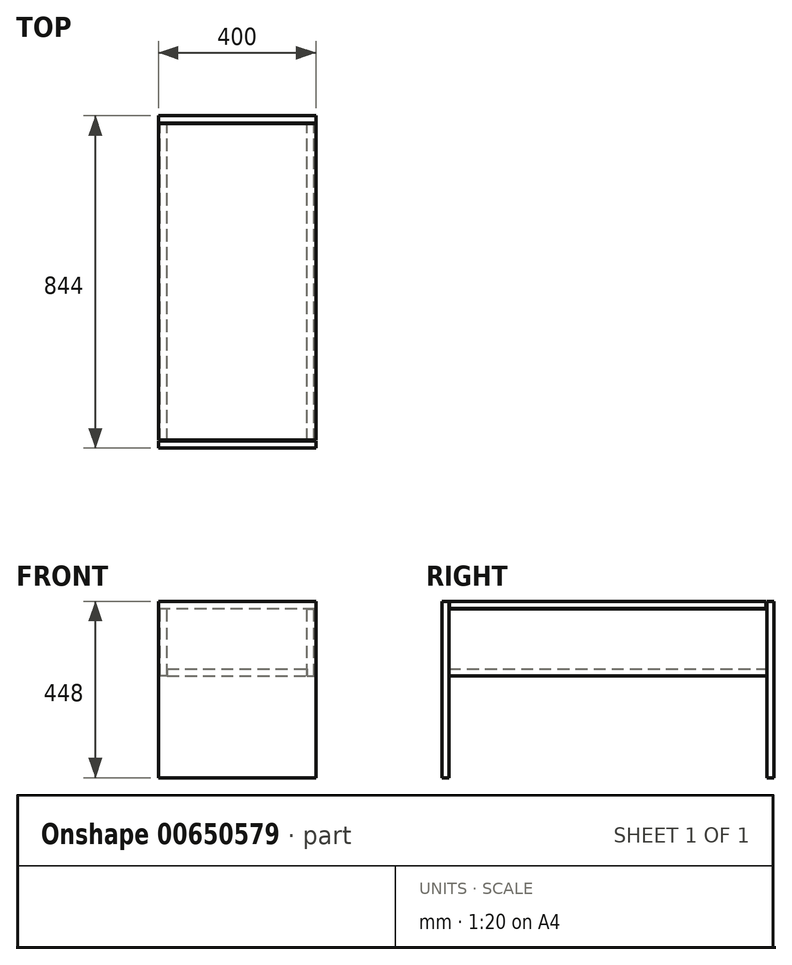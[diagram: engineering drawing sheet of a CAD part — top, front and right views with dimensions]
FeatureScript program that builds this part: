
annotation { "Feature Type Name" : "Feature", "Feature Type Description" : "" }
export const myFeature = defineFeature(function(context is Context, id is Id, definition is map)
    precondition{}
    {
        {
            var Q0;
            Q0=qCreatedBy(makeId("Top.planeOp"),FACE);
            var sketch = newSketch(context, id + "F0", { "sketchPlane" : qUnion([Q0])});
            skLineSegment(sketch, "E0.bottom", {"start": v(0, 0) * mm, "end": v(400, 0) * mm});
            skLineSegment(sketch, "E0.top", {"start": v(0, -18) * mm, "end": v(400, -18) * mm});
            skLineSegment(sketch, "E0.left", {"start": v(0, 0) * mm, "end": v(0, -18) * mm});
            skLineSegment(sketch, "E0.right", {"start": v(400, 0) * mm, "end": v(400, -18) * mm});
            skLineSegment(sketch, "E1.bottom", {"start": v(0, -826) * mm, "end": v(400, -826) * mm});
            skLineSegment(sketch, "E1.top", {"start": v(0, -844) * mm, "end": v(400, -844) * mm});
            skLineSegment(sketch, "E1.left", {"start": v(0, -826) * mm, "end": v(0, -844) * mm});
            skLineSegment(sketch, "E1.right", {"start": v(400, -826) * mm, "end": v(400, -844) * mm});
            skSolve(sketch);
        }
        {
            var Q0;
            Q0 = qSketchRegion(id + "F0", true);
            extrude(context, id + "F1", {"entities" : qUnion([Q0]), "depth" : 448 * mm, "offsetDistance" : 25 * mm});
        }
        {
            var Q0;
            Q0=makeQuery(id+"F1.opExtrude","SWEPT_FACE",FACE,{"disambiguationData":[OSD([sQuery(id+"F0.wireOp",EDGE,"E0.top")])]});
            var sketch = newSketch(context, id + "F2", { "sketchPlane" : qUnion([Q0])});
            skLineSegment(sketch, "E2.bottom", {"start": v(4, 429) * mm, "end": v(22, 429) * mm});
            skLineSegment(sketch, "E2.top", {"start": v(4, 259) * mm, "end": v(22, 259) * mm});
            skLineSegment(sketch, "E2.left", {"start": v(4, 429) * mm, "end": v(4, 259) * mm});
            skLineSegment(sketch, "E2.right", {"start": v(22, 429) * mm, "end": v(22, 259) * mm});
            skLineSegment(sketch, "E3.bottom", {"start": v(396, 429) * mm, "end": v(378, 429) * mm});
            skLineSegment(sketch, "E3.top", {"start": v(396, 259) * mm, "end": v(378, 259) * mm});
            skLineSegment(sketch, "E3.left", {"start": v(396, 429) * mm, "end": v(396, 259) * mm});
            skLineSegment(sketch, "E3.right", {"start": v(378, 429) * mm, "end": v(378, 259) * mm});
            skLineSegment(sketch, "E4", {"start": v(200, 448) * mm, "end": v(200, 0) * mm, "construction": true});
            skSolve(sketch);
        }
        {
            var Q0;
            Q0 = qSketchRegion(id + "F2", true);
            var Q1;
            Q1=makeQuery(id+"F1.opExtrude","SWEPT_FACE",FACE,{"disambiguationData":[OSD([sQuery(id+"F0.wireOp",EDGE,"E1.bottom")])]});
            extrude(context, id + "F3", {"entities" : qUnion([Q0]), "endBound" : BoundingType.UP_TO_SURFACE, "depth" : 25 * mm, "endBoundEntityFace" : qUnion([Q1]), "offsetDistance" : 25 * mm});
        }
        {
            var Q0;
            Q0=makeQuery(id+"F3.opExtrude","SWEPT_FACE",FACE,{"disambiguationData":[OSD([sQuery(id+"F2.wireOp",EDGE,"E3.top")])]});
            var sketch = newSketch(context, id + "F4", { "sketchPlane" : qUnion([Q0])});
            skLineSegment(sketch, "E5.bottom", {"start": v(22, 826) * mm, "end": v(378, 826) * mm});
            skLineSegment(sketch, "E5.top", {"start": v(22, 18) * mm, "end": v(378, 18) * mm});
            skLineSegment(sketch, "E5.left", {"start": v(378, 826) * mm, "end": v(378, 18) * mm});
            skLineSegment(sketch, "E5.right", {"start": v(22, 826) * mm, "end": v(22, 18) * mm});
            skSolve(sketch);
        }
        {
            var Q0;
            Q0 = qSketchRegion(id + "F4", true);
            extrude(context, id + "F5", {"entities" : qUnion([Q0]), "oppositeDirection" : true, "depth" : 18 * mm, "offsetDistance" : 25 * mm});
        }
        {
            var Q0;
            Q0=makeQuery(id+"F1.opExtrude","CAP_FACE",FACE,{"disambiguationData":[OSD([sQuery(id+"F0.wireOp",EDGE,"E0.bottom"),sQuery(id+"F0.wireOp",EDGE,"E0.top"),sQuery(id+"F0.wireOp",EDGE,"E0.left"),sQuery(id+"F0.wireOp",EDGE,"E0.right")])],"isStart":false});
            var sketch = newSketch(context, id + "F6", { "sketchPlane" : qUnion([Q0])});
            skLineSegment(sketch, "E6.bottom", {"start": v(0, -20) * mm, "end": v(400, -20) * mm});
            skLineSegment(sketch, "E6.top", {"start": v(0, -824) * mm, "end": v(400, -824) * mm});
            skLineSegment(sketch, "E6.left", {"start": v(0, -20) * mm, "end": v(0, -824) * mm});
            skLineSegment(sketch, "E6.right", {"start": v(400, -20) * mm, "end": v(400, -824) * mm});
            skLineSegment(sketch, "E7", {"start": v(22, -422) * mm, "end": v(400, -422) * mm, "construction": true});
            skSolve(sketch);
        }
        {
            var Q0;
            Q0 = qSketchRegion(id + "F6", true);
            extrude(context, id + "F7", {"entities" : qUnion([Q0]), "oppositeDirection" : true, "depth" : 18 * mm, "offsetDistance" : 25 * mm});
        }
    });
